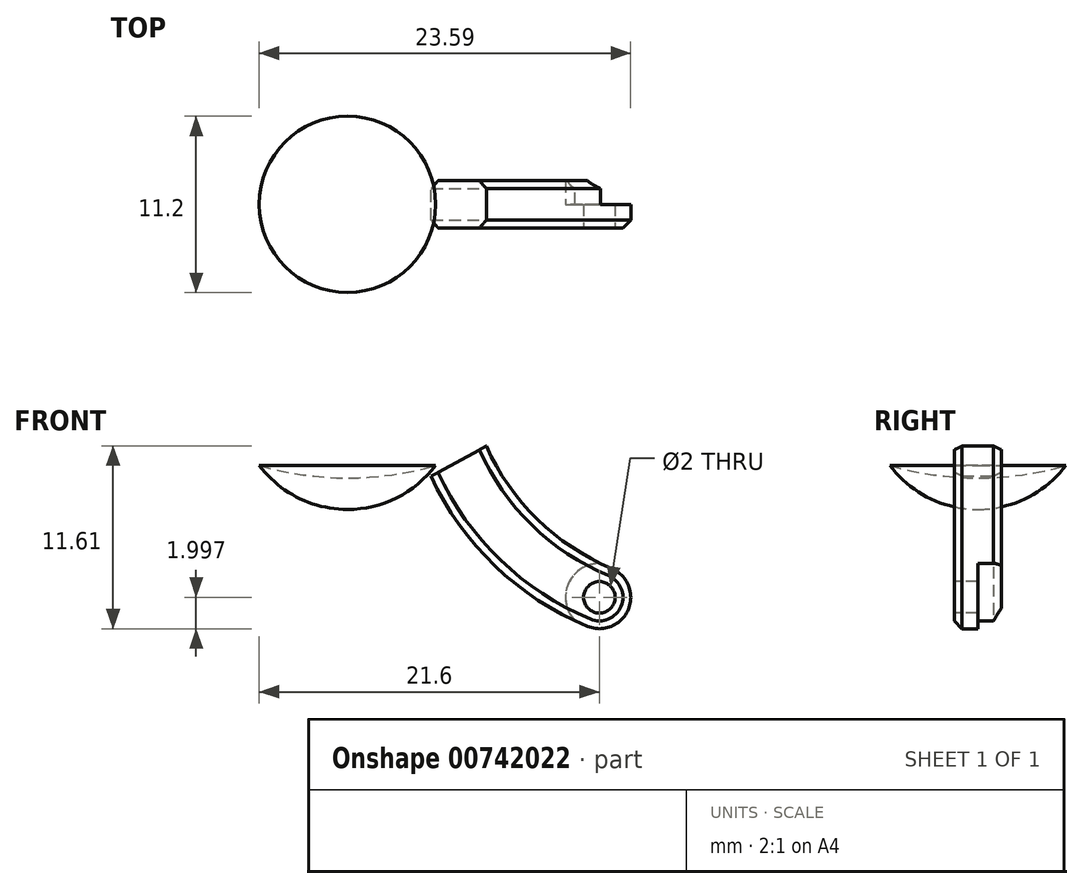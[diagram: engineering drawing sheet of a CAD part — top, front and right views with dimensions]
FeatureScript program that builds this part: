
annotation { "Feature Type Name" : "Feature", "Feature Type Description" : "" }
export const myFeature = defineFeature(function(context is Context, id is Id, definition is map)
    precondition{}
    {
        {
            var Q0;
            Q0=qCreatedBy(makeId("Top.planeOp"),FACE);
            var sketch = newSketch(context, id + "F0", { "sketchPlane" : qUnion([Q0])});
            skCircle(sketch, "E0", {"center": v(0, 0) * mm, "radius": 20 * mm});
            skLineSegment(sketch, "E1", {"start": v(0, 20) * mm, "end": v(0, -20) * mm});
            skSolve(sketch);
        }
        {
            var Q0;
            {var subQ0=sQuery(id+"F0.wireOp",EDGE,"E1");Q0=makeQuery(id+"F0.imprint","IMPRINT",FACE,{"disambiguationData":[TD([[makeQuery(id+"F0.imprint","IMPRINT",EDGE,{"derivedFrom":subQ0}),-1.0]])]});}
            var Q1;
            Q1=sQuery(id+"F0.wireOp",EDGE,"E1");
            revolve(context, id + "F1", {"surfaceOperationType" : NewSurfaceOperationType.NEW, "entities" : qUnion([Q0]), "axis" : qUnion([Q1]), "revolveType" : RevolveType.FULL});
        }
        {
            var Q0;
            Q0=qCreatedBy(makeId("Front.planeOp"),FACE);
            var sketch = newSketch(context, id + "F2", { "sketchPlane" : qUnion([Q0])});
            skLineSegment(sketch, "E2", {"start": v(0, -20) * mm, "end": v(0, -22) * mm});
            skCircle(sketch, "E3", {"center": v(0, 0) * mm, "radius": 20 * mm});
            skCircle(sketch, "E4", {"center": v(0, -15) * mm, "radius": 7 * mm});
            skPoint(sketch, "E5", {"position": v(0, -21) * mm});
            skCircle(sketch, "E6", {"center": v(0, -6) * mm, "radius": 15 * mm});
            skSolve(sketch);
        }
        {
            var Q0;
            {var subQ0=sQuery(id+"F2.wireOp",EDGE,"E6");var subQ1=sQuery(id+"F2.wireOp",EDGE,"E3");var subQ2=makeQuery(id+"F2.imprint","INTERSECT",VERTEX,{"disambiguationData":[OD(0.0)],"derivedFrom":[subQ1,subQ0]});Q0=makeQuery(id+"F2.imprint","IMPRINT",FACE,{"disambiguationData":[TD([[makeQuery(id+"F2.imprint","IMPRINT",EDGE,{"disambiguationData":[TD([[subQ2,-1.0]])],"derivedFrom":subQ1}),-1.0]])]});}
            var Q1;
            {var subQ0=sQuery(id+"F2.wireOp",EDGE,"E3");var subQ1=sQuery(id+"F2.wireOp",EDGE,"E2");var subQ2=makeQuery(id+"F2.imprint","INTERSECT",VERTEX,{"derivedFrom":[subQ1,subQ0]});Q1=makeQuery(id+"F2.imprint","IMPRINT",FACE,{"disambiguationData":[TD([[makeQuery(id+"F2.imprint","IMPRINT",EDGE,{"disambiguationData":[TD([[subQ2,-1.0]])],"derivedFrom":subQ1}),-1.0]])]});}
            var Q2;
            {var subQ0=sQuery(id+"F2.wireOp",EDGE,"E4");var subQ1=sQuery(id+"F2.wireOp",EDGE,"E2");var subQ2=makeQuery(id+"F2.imprint","INTERSECT",VERTEX,{"derivedFrom":[subQ1,subQ0]});Q2=makeQuery(id+"F2.imprint","IMPRINT",FACE,{"disambiguationData":[TD([[makeQuery(id+"F2.imprint","IMPRINT",EDGE,{"disambiguationData":[TD([[subQ2,1.0]])],"derivedFrom":subQ1}),-1.0]])]});}
            var Q3;
            Q3=sQuery(id+"F2.wireOp",EDGE,"E2");
            revolve(context, id + "F3", {"operationType" : NewBodyOperationType.ADD, "surfaceOperationType" : NewSurfaceOperationType.NEW, "entities" : qUnion([Q0, Q1, Q2]), "axis" : qUnion([Q3]), "revolveType" : RevolveType.FULL});
        }
        {
            var Q0;
            Q0=qCreatedBy(makeId("Top.planeOp"),FACE);
            var sketch = newSketch(context, id + "F4", { "sketchPlane" : qUnion([Q0])});
            skLineSegment(sketch, "E7", {"start": v(0, 20) * mm, "end": v(0, -20) * mm});
            skArc(sketch, "E8", {"start": v(0, -20) * mm, "mid": v(20, 0) * mm, "end": v(0, 20) * mm});
            skSolve(sketch);
        }
        {
            var Q0;
            Q0 = qSketchRegion(id + "F4", true);
            var Q1;
            Q1=sQuery(id+"F4.wireOp",EDGE,"E7");
            revolve(context, id + "F5", {"operationType" : NewBodyOperationType.REMOVE, "surfaceOperationType" : NewSurfaceOperationType.NEW, "entities" : qUnion([Q0]), "axis" : qUnion([Q1]), "revolveType" : RevolveType.FULL, "oppositeDirection" : true});
        }
        {
            var Q0;
            Q0=qCreatedBy(makeId("Front.planeOp"),FACE);
            var sketch = newSketch(context, id + "F6", { "sketchPlane" : qUnion([Q0])});
            skArc(sketch, "E9", {"start": v(8.82, -17.97) * mm, "mid": v(12.05, -22.62) * mm, "end": v(16.77, -25.74) * mm});
            skArc(sketch, "E10", {"start": v(5.3, -19.89) * mm, "mid": v(9.38, -25.59) * mm, "end": v(15.23, -29.42) * mm});
            skArc(sketch, "E11", {"start": v(15.23, -29.42) * mm, "mid": v(17.84, -28.35) * mm, "end": v(16.77, -25.74) * mm});
            skLineSegment(sketch, "E12.0", {"start": v(-9.53, -17.58) * mm, "end": v(9.53, -17.58) * mm});
            skPoint(sketch, "E13", {"position": v(0, -17.58) * mm});
            skLineSegment(sketch, "E14", {"start": v(8.82, -17.97) * mm, "end": v(5.3, -19.89) * mm});
            skLineSegment(sketch, "E15", {"start": v(4.6, -20.28) * mm, "end": v(9.53, -17.58) * mm});
            skLineSegment(sketch, "E16.0", {"start": v(-4.6, -20.28) * mm, "end": v(4.6, -20.28) * mm});
            skLineSegment(sketch, "E17", {"start": v(7.06, -18.93) * mm, "end": v(7.06, -18.93) * mm});
            skSolve(sketch);
        }
        {
            var Q0;
            Q0=makeQuery(id+"F6.imprint","IMPRINT",FACE,{"disambiguationData":[TD([[makeQuery(id+"F6.imprint","IMPRINT",EDGE,{"derivedFrom":sQuery(id+"F6.wireOp",EDGE,"E9")}),-1.0]])]});
            extrude(context, id + "F7", {"entities" : qUnion([Q0]), "operationType" : NewBodyOperationType.ADD, "endBound" : BoundingType.SYMMETRIC, "depth" : 3 * mm, "offsetDistance" : 25 * mm});
        }
        {
            var Q0;
            Q0=makeQuery(id+"F7.opExtrude","CAP_EDGE",EDGE,{"disambiguationData":[OSD([sQuery(id+"F6.wireOp",EDGE,"E10")])],"isStart":true});
            var Q1;
            Q1=makeQuery(id+"F7.opExtrude","CAP_EDGE",EDGE,{"disambiguationData":[OSD([sQuery(id+"F6.wireOp",EDGE,"E11")])],"isStart":true});
            var Q2;
            Q2=makeQuery(id+"F7.opExtrude","CAP_EDGE",EDGE,{"disambiguationData":[OSD([sQuery(id+"F6.wireOp",EDGE,"E9")])],"isStart":true});
            var Q3;
            Q3=makeQuery(id+"F7.opExtrude","CAP_EDGE",EDGE,{"disambiguationData":[OSD([sQuery(id+"F6.wireOp",EDGE,"E9")])],"isStart":false});
            var Q4;
            Q4=makeQuery(id+"F7.opExtrude","CAP_EDGE",EDGE,{"disambiguationData":[OSD([sQuery(id+"F6.wireOp",EDGE,"E11")])],"isStart":false});
            var Q5;
            Q5=makeQuery(id+"F7.opExtrude","CAP_EDGE",EDGE,{"disambiguationData":[OSD([sQuery(id+"F6.wireOp",EDGE,"E10")])],"isStart":false});
            chamfer(context, id + "F8", {"entities" : qUnion([Q0, Q1, Q2, Q3, Q4, Q5]), "width" : 0.5 * mm});
        }
        {
            var Q0;
            Q0=qCreatedBy(makeId("Front.planeOp"),FACE);
            var sketch = newSketch(context, id + "F9", { "sketchPlane" : qUnion([Q0])});
            skArc(sketch, "E18.0", {"start": v(14.42, -28.8) * mm, "mid": v(17.5, -28.9) * mm, "end": v(17.02, -25.87) * mm});
            skCircle(sketch, "E19", {"center": v(16, -27.58) * mm, "radius": 2 * mm, "construction": true});
            skCircle(sketch, "E20", {"center": v(16, -27.58) * mm, "radius": 2.15 * mm});
            skSolve(sketch);
        }
        {
            var Q0;
            Q0 = qSketchRegion(id + "F9", true);
            extrude(context, id + "F10", {"entities" : qUnion([Q0]), "operationType" : NewBodyOperationType.REMOVE, "endBound" : BoundingType.UP_TO_NEXT, "oppositeDirection" : true, "depth" : 1.2 * mm, "offsetDistance" : 25 * mm});
        }
        {
            var Q0;
            Q0=makeQuery(id+"F7.opExtrude","CAP_FACE",FACE,{"disambiguationData":[OSD([sQuery(id+"F6.wireOp",EDGE,"E9"),sQuery(id+"F6.wireOp",EDGE,"E10"),sQuery(id+"F6.wireOp",EDGE,"E11"),sQuery(id+"F6.wireOp",EDGE,"E14")])],"isStart":false});
            var sketch = newSketch(context, id + "F11", { "sketchPlane" : qUnion([Q0])});
            skCircle(sketch, "E21", {"center": v(16, -27.58) * mm, "radius": 1 * mm});
            skSolve(sketch);
        }
        {
            var Q0;
            Q0 = qSketchRegion(id + "F11", true);
            var Q1;
            Q1=makeQuery(id+"F7.opExtrude","CAP_FACE",FACE,{"disambiguationData":[OSD([sQuery(id+"F6.wireOp",EDGE,"E9"),sQuery(id+"F6.wireOp",EDGE,"E10"),sQuery(id+"F6.wireOp",EDGE,"E11"),sQuery(id+"F6.wireOp",EDGE,"E14")])],"isStart":true});
            extrude(context, id + "F12", {"entities" : qUnion([Q0]), "operationType" : NewBodyOperationType.REMOVE, "endBound" : BoundingType.UP_TO_SURFACE, "oppositeDirection" : true, "depth" : 25 * mm, "endBoundEntityFace" : qUnion([Q1]), "offsetDistance" : 25 * mm});
        }
    });
